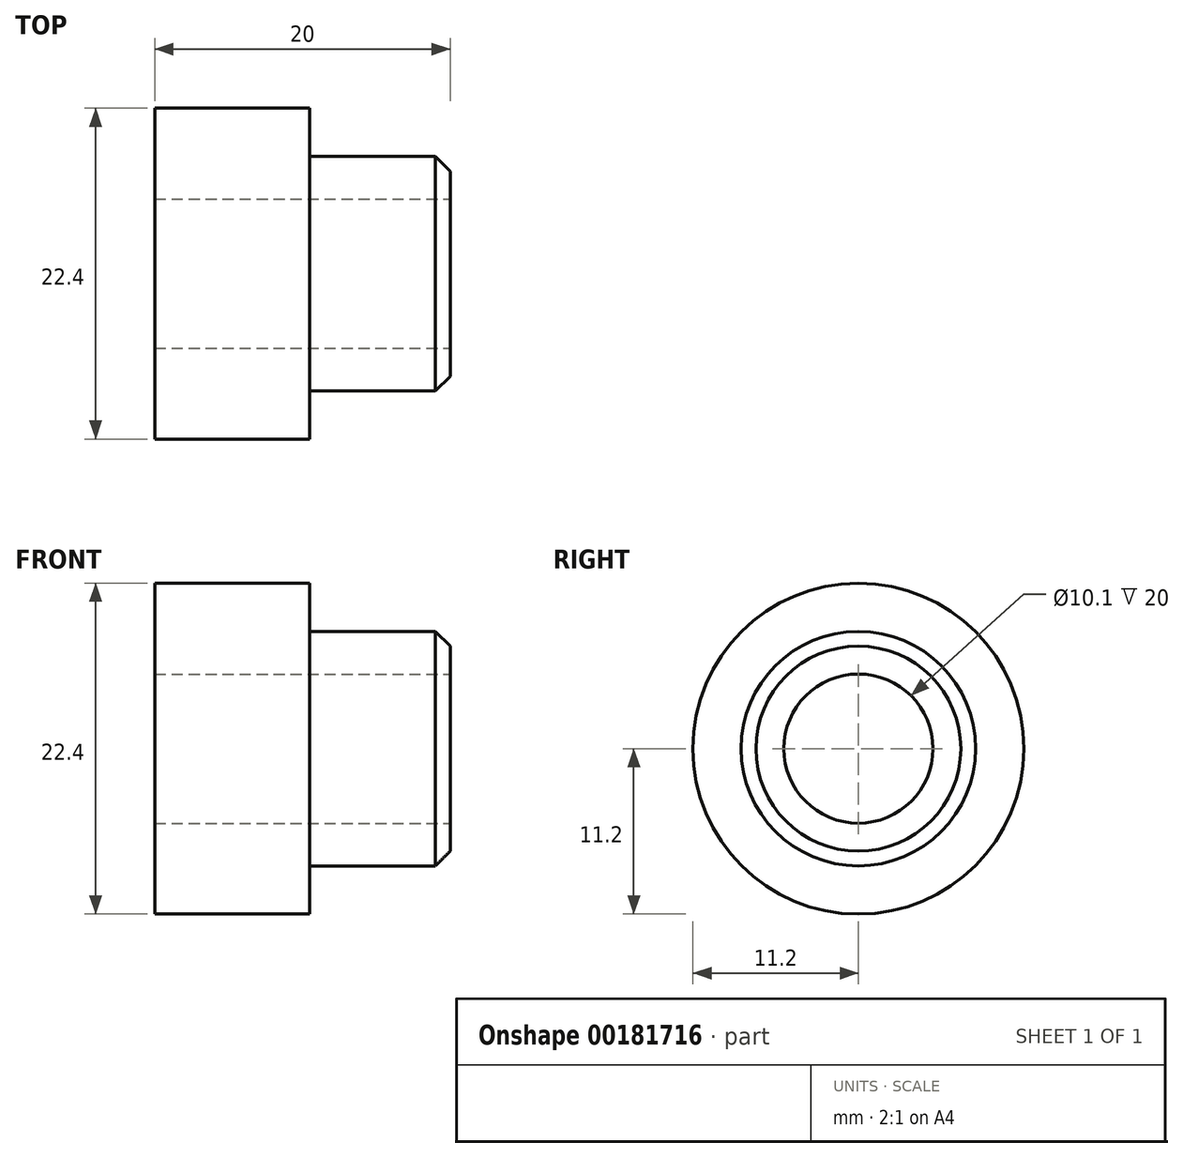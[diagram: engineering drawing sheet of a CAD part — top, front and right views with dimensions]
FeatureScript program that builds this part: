
annotation { "Feature Type Name" : "Feature", "Feature Type Description" : "" }
export const myFeature = defineFeature(function(context is Context, id is Id, definition is map)
    precondition{}
    {
        {
            var Q0;
            Q0=qCreatedBy(makeId("Right.planeOp"),FACE);
            var sketch = newSketch(context, id + "F0", { "sketchPlane" : qUnion([Q0])});
            skCircle(sketch, "E0", {"center": v(0, 0) * mm, "radius": 11.2 * mm});
            skSolve(sketch);
        }
        {
            var Q0;
            Q0=makeQuery(id+"F0.imprint","IMPRINT",FACE,{"disambiguationData":[TD([[makeQuery(id+"F0.imprint","IMPRINT",EDGE,{"derivedFrom":sQuery(id+"F0.wireOp",EDGE,"E0")}),1.0]])]});
            extrude(context, id + "F1", {"entities" : qUnion([Q0]), "depth" : 10.47 * mm});
        }
        {
            var Q0;
            Q0=makeQuery(id+"F1.opExtrude","CAP_FACE",FACE,{"disambiguationData":[OSD([sQuery(id+"F0.wireOp",EDGE,"E0")])],"isStart":false});
            var sketch = newSketch(context, id + "F2", { "sketchPlane" : qUnion([Q0])});
            skCircle(sketch, "E1", {"center": v(0, 0) * mm, "radius": 7.94 * mm});
            skSolve(sketch);
        }
        {
            var Q0;
            Q0 = qSketchRegion(id + "F2", true);
            extrude(context, id + "F3", {"entities" : qUnion([Q0]), "operationType" : NewBodyOperationType.ADD, "depth" : 9.52 * mm});
        }
        {
            var Q0;
            Q0=makeQuery(id+"F3.opExtrude","CAP_FACE",FACE,{"disambiguationData":[OSD([sQuery(id+"F2.wireOp",EDGE,"E1")])],"isStart":false});
            var sketch = newSketch(context, id + "F4", { "sketchPlane" : qUnion([Q0])});
            skCircle(sketch, "E2", {"center": v(0, 0) * mm, "radius": 5.08 * mm});
            skSolve(sketch);
        }
        {
            var Q0;
            Q0=sQuery(id+"F4.wireOp",VERTEX,"E2.center");
            var Q1;
            Q1=makeQuery(id+"F1.opExtrude","SWEPT_BODY",BODY,{"disambiguationData":[OSD([sQuery(id+"F0.wireOp",EDGE,"E0")])]});
            hole(context, id + "F5", {"style" : HoleStyle.SIMPLE, "endStyle" : HoleEndStyle.THROUGH, "holeDiameter" : 10.1 * mm, "locations" : qUnion([Q0]), "scope" : qUnion([Q1]), "isTappedThrough" : true});
        }
        {
            var Q0;
            Q0=makeQuery(id+"F3.opExtrude","CAP_EDGE",EDGE,{"disambiguationData":[OSD([sQuery(id+"F2.wireOp",EDGE,"E1")])],"isStart":false});
            chamfer(context, id + "F6", {"entities" : qUnion([Q0]), "width" : 1 * mm, "tangentPropagation" : true});
        }
    });
